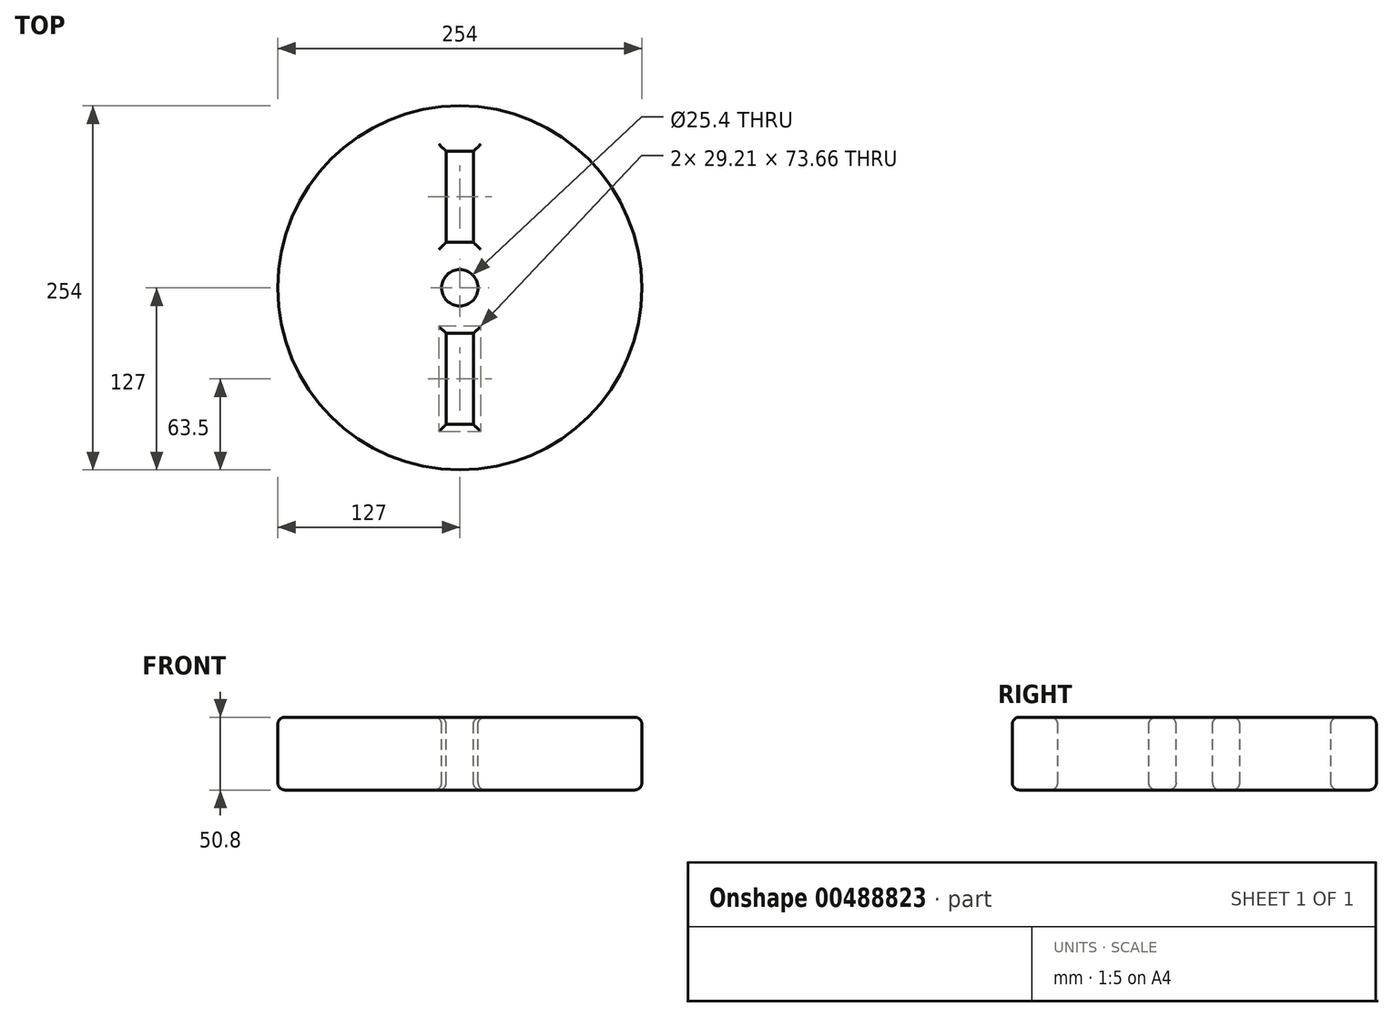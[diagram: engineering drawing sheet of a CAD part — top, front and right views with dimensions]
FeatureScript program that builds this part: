
annotation { "Feature Type Name" : "Feature", "Feature Type Description" : "" }
export const myFeature = defineFeature(function(context is Context, id is Id, definition is map)
    precondition{}
    {
        {
            var Q0;
            Q0=qCreatedBy(makeId("Front.planeOp"),FACE);
            var sketch = newSketch(context, id + "F0", { "sketchPlane" : qUnion([Q0])});
            skLineSegment(sketch, "E0.bottom", {"start": v(0, 0) * mm, "end": v(127, 0) * mm});
            skLineSegment(sketch, "E0.top", {"start": v(0, 50.8) * mm, "end": v(127, 50.8) * mm});
            skLineSegment(sketch, "E0.left", {"start": v(0, 0) * mm, "end": v(0, 50.8) * mm});
            skLineSegment(sketch, "E0.right", {"start": v(127, 0) * mm, "end": v(127, 50.8) * mm});
            skSolve(sketch);
        }
        {
            var Q0;
            Q0 = qSketchRegion(id + "F0", true);
            var Q1;
            Q1=sQuery(id+"F0.wireOp",EDGE,"E0.left");
            revolve(context, id + "F1", {"entities" : qUnion([Q0]), "axis" : qUnion([Q1]), "revolveType" : RevolveType.FULL});
        }
        {
            var Q0;
            Q0=makeQuery(id+"F1.opRevolve","SWEPT_FACE",FACE,{"disambiguationData":[OSD([sQuery(id+"F0.wireOp",EDGE,"E0.top")])]});
            var sketch = newSketch(context, id + "F2", { "sketchPlane" : qUnion([Q0])});
            skLineSegment(sketch, "E1", {"start": v(0, 0) * mm, "end": v(0, 127) * mm, "construction": true});
            skLineSegment(sketch, "E2", {"start": v(0, 0) * mm, "end": v(0, -127) * mm, "construction": true});
            skLineSegment(sketch, "E3.bottom", {"start": v(9.53, -95.25) * mm, "end": v(-9.52, -95.25) * mm});
            skLineSegment(sketch, "E3.top", {"start": v(9.53, -31.75) * mm, "end": v(-9.52, -31.75) * mm});
            skLineSegment(sketch, "E3.left", {"start": v(9.53, -95.25) * mm, "end": v(9.53, -31.75) * mm});
            skLineSegment(sketch, "E3.right", {"start": v(-9.52, -95.25) * mm, "end": v(-9.52, -31.75) * mm});
            skPoint(sketch, "E3.middle", {"position": v(0, -63.5) * mm});
            skLineSegment(sketch, "E4.1.2", {"start": v(0, 0) * mm, "end": v(-127, 0) * mm, "construction": true});
            skLineSegment(sketch, "E4.2.1", {"start": v(0, 0) * mm, "end": v(-127, 0) * mm, "construction": true});
            skLineSegment(sketch, "E4.2.3", {"start": v(0, 0) * mm, "end": v(127, 0) * mm, "construction": true});
            skLineSegment(sketch, "E4.3.0", {"start": v(0, 0) * mm, "end": v(-127, 0) * mm, "construction": true});
            skPoint(sketch, "E4.center", {"position": v(0, 0) * mm});
            skLineSegment(sketch, "E5.MirrorCS", {"start": v(-9.52, 95.25) * mm, "end": v(-9.52, 31.75) * mm});
            skLineSegment(sketch, "E6.MirrorCS", {"start": v(9.53, 95.25) * mm, "end": v(9.53, 31.75) * mm});
            skLineSegment(sketch, "E7.MirrorCS", {"start": v(9.53, 31.75) * mm, "end": v(-9.52, 31.75) * mm});
            skLineSegment(sketch, "E8.MirrorCS", {"start": v(9.53, 95.25) * mm, "end": v(-9.52, 95.25) * mm});
            skSolve(sketch);
        }
        {
            var Q0;
            Q0=makeQuery(id+"F2.imprint","IMPRINT",FACE,{"disambiguationData":[TD([[makeQuery(id+"F2.imprint","IMPRINT",EDGE,{"derivedFrom":sQuery(id+"F2.wireOp",EDGE,"E5.MirrorCS")}),1.0]])]});
            var Q1;
            Q1=makeQuery(id+"F2.imprint","IMPRINT",FACE,{"disambiguationData":[TD([[makeQuery(id+"F2.imprint","IMPRINT",EDGE,{"derivedFrom":sQuery(id+"F2.wireOp",EDGE,"E3.bottom")}),-1.0]])]});
            extrude(context, id + "F3", {"entities" : qUnion([Q0, Q1]), "operationType" : NewBodyOperationType.REMOVE, "endBound" : BoundingType.THROUGH_ALL, "oppositeDirection" : true, "depth" : 25.4 * mm});
        }
        {
            var Q0;
            Q0=makeQuery(id+"F1.opRevolve","SWEPT_FACE",FACE,{"disambiguationData":[OSD([sQuery(id+"F0.wireOp",EDGE,"E0.top")])]});
            var sketch = newSketch(context, id + "F4", { "sketchPlane" : qUnion([Q0])});
            skCircle(sketch, "E9", {"center": v(0, 0) * mm, "radius": 12.7 * mm});
            skSolve(sketch);
        }
        {
            var Q0;
            Q0=makeQuery(id+"F4.imprint","IMPRINT",FACE,{"disambiguationData":[TD([[makeQuery(id+"F4.imprint","IMPRINT",EDGE,{"derivedFrom":sQuery(id+"F4.wireOp",EDGE,"E9")}),1.0]])]});
            extrude(context, id + "F5", {"entities" : qUnion([Q0]), "operationType" : NewBodyOperationType.REMOVE, "endBound" : BoundingType.THROUGH_ALL, "oppositeDirection" : true, "depth" : 25.4 * mm});
        }
        {
            var Q0;
            Q0=makeQuery(id+"F1.opRevolve","SWEPT_EDGE",EDGE,{"disambiguationData":[OSD([sQuery(id+"F0.wireOp",EDGE,"E0.top"),sQuery(id+"F0.wireOp",EDGE,"E0.right")])]});
            var Q1;
            Q1=makeQuery(id+"F3.boolean.opBoolean","COPY",EDGE,{"derivedFrom":makeQuery(id+"F3.opExtrude","CAP_EDGE",EDGE,{"disambiguationData":[OSD([sQuery(id+"F2.wireOp",EDGE,"E3.left")])],"isStart":true})});
            var Q2;
            Q2=makeQuery(id+"F1.opRevolve","SWEPT_FACE",FACE,{"disambiguationData":[OSD([sQuery(id+"F0.wireOp",EDGE,"E0.top")])]});
            var Q3;
            Q3=makeQuery(id+"F1.opRevolve","SWEPT_EDGE",EDGE,{"disambiguationData":[OSD([sQuery(id+"F0.wireOp",EDGE,"E0.bottom"),sQuery(id+"F0.wireOp",EDGE,"E0.right")])]});
            var Q4;
            Q4=makeQuery(id+"F3.boolean.opBoolean","INTERSECT",EDGE,{"derivedFrom":[makeQuery(id+"F1.opRevolve","SWEPT_FACE",FACE,{"disambiguationData":[OSD([sQuery(id+"F0.wireOp",EDGE,"E0.bottom")])]}),makeQuery(id+"F3.opExtrude","SWEPT_FACE",FACE,{"disambiguationData":[OSD([sQuery(id+"F2.wireOp",EDGE,"E3.left")])]})]});
            var Q5;
            Q5=makeQuery(id+"F3.boolean.opBoolean","INTERSECT",EDGE,{"derivedFrom":[makeQuery(id+"F1.opRevolve","SWEPT_FACE",FACE,{"disambiguationData":[OSD([sQuery(id+"F0.wireOp",EDGE,"E0.bottom")])]}),makeQuery(id+"F3.opExtrude","SWEPT_FACE",FACE,{"disambiguationData":[OSD([sQuery(id+"F2.wireOp",EDGE,"E3.bottom")])]})]});
            var Q6;
            Q6=makeQuery(id+"F3.boolean.opBoolean","INTERSECT",EDGE,{"derivedFrom":[makeQuery(id+"F1.opRevolve","SWEPT_FACE",FACE,{"disambiguationData":[OSD([sQuery(id+"F0.wireOp",EDGE,"E0.bottom")])]}),makeQuery(id+"F3.opExtrude","SWEPT_FACE",FACE,{"disambiguationData":[OSD([sQuery(id+"F2.wireOp",EDGE,"E3.right")])]})]});
            var Q7;
            Q7=makeQuery(id+"F3.boolean.opBoolean","INTERSECT",EDGE,{"derivedFrom":[makeQuery(id+"F1.opRevolve","SWEPT_FACE",FACE,{"disambiguationData":[OSD([sQuery(id+"F0.wireOp",EDGE,"E0.bottom")])]}),makeQuery(id+"F3.opExtrude","SWEPT_FACE",FACE,{"disambiguationData":[OSD([sQuery(id+"F2.wireOp",EDGE,"E3.top")])]})]});
            var Q8;
            Q8=makeQuery(id+"F5.boolean.opBoolean","INTERSECT",EDGE,{"derivedFrom":[makeQuery(id+"F1.opRevolve","SWEPT_FACE",FACE,{"disambiguationData":[OSD([sQuery(id+"F0.wireOp",EDGE,"E0.bottom")])]}),makeQuery(id+"F5.opExtrude","SWEPT_FACE",FACE,{"disambiguationData":[OSD([sQuery(id+"F4.wireOp",EDGE,"E9")])]})]});
            var Q9;
            Q9=makeQuery(id+"F3.boolean.opBoolean","INTERSECT",EDGE,{"derivedFrom":[makeQuery(id+"F1.opRevolve","SWEPT_FACE",FACE,{"disambiguationData":[OSD([sQuery(id+"F0.wireOp",EDGE,"E0.bottom")])]}),makeQuery(id+"F3.opExtrude","SWEPT_FACE",FACE,{"disambiguationData":[OSD([sQuery(id+"F2.wireOp",EDGE,"E7.MirrorCS")])]})]});
            var Q10;
            Q10=makeQuery(id+"F3.boolean.opBoolean","INTERSECT",EDGE,{"derivedFrom":[makeQuery(id+"F1.opRevolve","SWEPT_FACE",FACE,{"disambiguationData":[OSD([sQuery(id+"F0.wireOp",EDGE,"E0.bottom")])]}),makeQuery(id+"F3.opExtrude","SWEPT_FACE",FACE,{"disambiguationData":[OSD([sQuery(id+"F2.wireOp",EDGE,"E6.MirrorCS")])]})]});
            var Q11;
            Q11=makeQuery(id+"F3.boolean.opBoolean","INTERSECT",EDGE,{"derivedFrom":[makeQuery(id+"F1.opRevolve","SWEPT_FACE",FACE,{"disambiguationData":[OSD([sQuery(id+"F0.wireOp",EDGE,"E0.bottom")])]}),makeQuery(id+"F3.opExtrude","SWEPT_FACE",FACE,{"disambiguationData":[OSD([sQuery(id+"F2.wireOp",EDGE,"E5.MirrorCS")])]})]});
            var Q12;
            Q12=makeQuery(id+"F3.boolean.opBoolean","INTERSECT",EDGE,{"derivedFrom":[makeQuery(id+"F1.opRevolve","SWEPT_FACE",FACE,{"disambiguationData":[OSD([sQuery(id+"F0.wireOp",EDGE,"E0.bottom")])]}),makeQuery(id+"F3.opExtrude","SWEPT_FACE",FACE,{"disambiguationData":[OSD([sQuery(id+"F2.wireOp",EDGE,"E8.MirrorCS")])]})]});
            fillet(context, id + "F6", {"entities" : qUnion([Q0, Q1, Q2, Q3, Q4, Q5, Q6, Q7, Q8, Q9, Q10, Q11, Q12]), "radius" : 5.08 * mm, "tangentPropagation" : true, "allowEdgeOverflow" : false});
        }
    });
